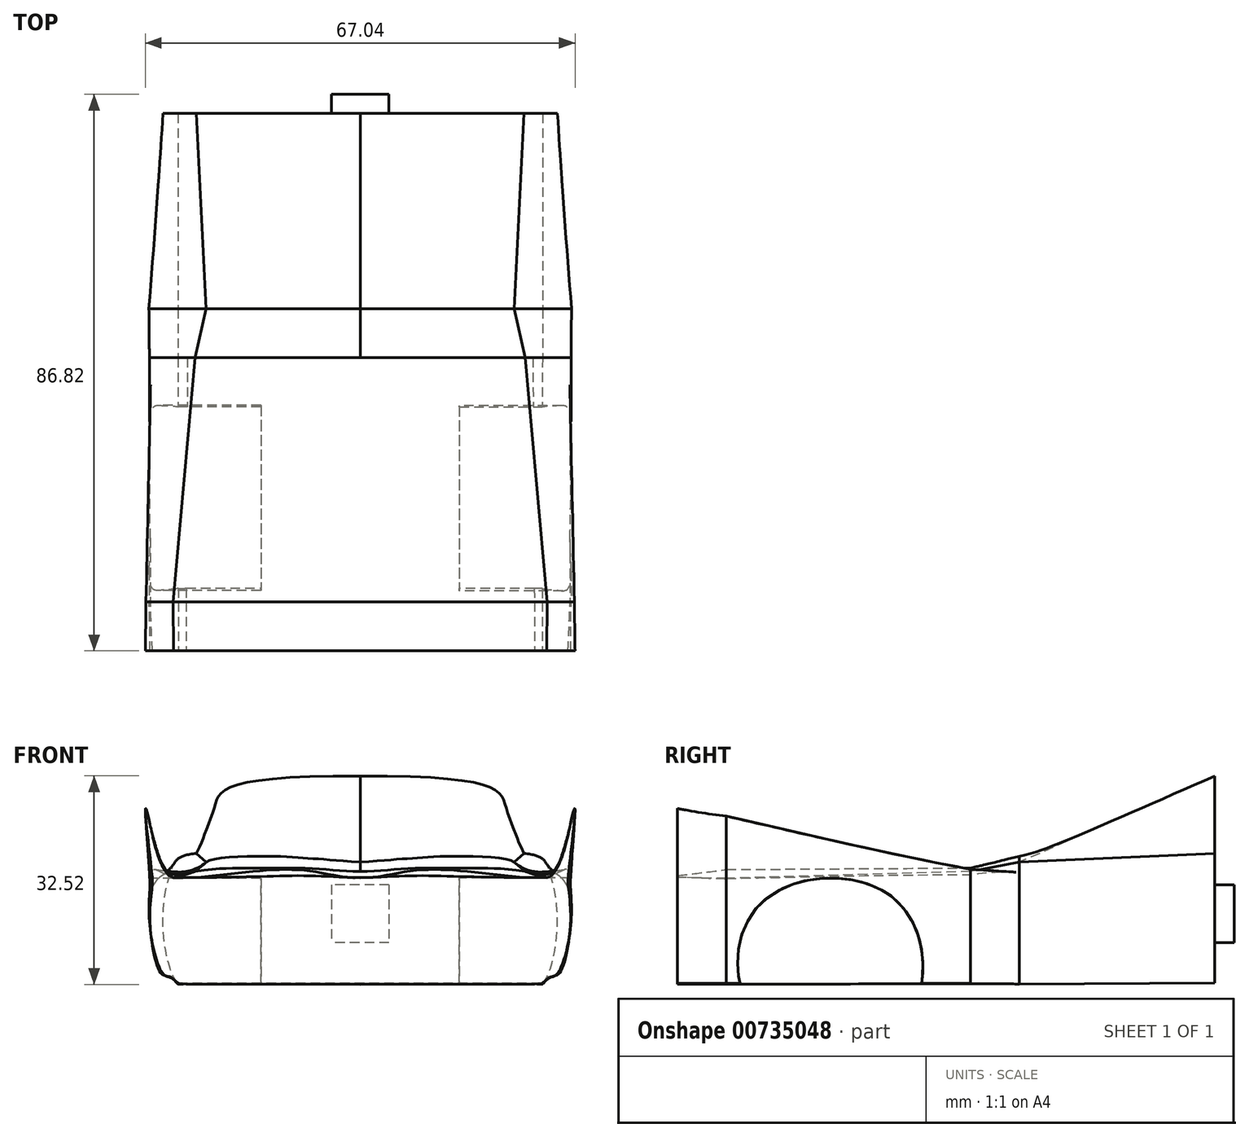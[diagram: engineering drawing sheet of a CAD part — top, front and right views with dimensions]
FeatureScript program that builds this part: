
annotation { "Feature Type Name" : "Feature", "Feature Type Description" : "" }
export const myFeature = defineFeature(function(context is Context, id is Id, definition is map)
    precondition{}
    {
        {
            var Q0;
            Q0=qCreatedBy(makeId("Front.planeOp"),FACE);
            var sketch = newSketch(context, id + "F0", { "sketchPlane" : qUnion([Q0])});
            skLineSegment(sketch, "E0", {"start": v(0, -180.47) * mm, "end": v(448.71, -180.47) * mm});
            skLineSegment(sketch, "E1", {"start": v(0, 357.9) * mm, "end": v(0, -180.47) * mm});
            skFitSpline(sketch, "E2", {"points": [v(448.71, -180.47) * mm, v(474.16, -180.47) * mm, v(512.73, -30.33) * mm, v(489.93, 116.8) * mm, v(425.94, 156.85) * mm], "startDerivative": vector(218.59, -88.61) * mm, "endDerivative": vector(-639.63, 77.65) * mm});
            skFitSpline(sketch, "E3", {"points": [v(425.94, 156.85) * mm, v(403.5, 209.2) * mm, v(380.6, 271.65) * mm, v(367.32, 306.69) * mm, v(0, 357.9) * mm], "startDerivative": vector(-217.52, 427.03) * mm, "endDerivative": vector(-1727.63, -7.94) * mm});
            skFitSpline(sketch, "E4.MirrorCS", {"points": [v(-448.71, -180.47) * mm, v(-474.16, -180.47) * mm, v(-512.73, -30.33) * mm, v(-489.93, 116.8) * mm, v(-425.94, 156.85) * mm], "startDerivative": vector(-218.59, -88.61) * mm, "endDerivative": vector(639.63, 77.65) * mm});
            skLineSegment(sketch, "E5.MirrorCS", {"start": v(0, -180.47) * mm, "end": v(-448.71, -180.47) * mm});
            skFitSpline(sketch, "E6.MirrorCS", {"points": [v(-425.94, 156.85) * mm, v(-403.5, 209.2) * mm, v(-380.6, 271.65) * mm, v(-367.32, 306.69) * mm, v(0, 357.9) * mm], "startDerivative": vector(217.52, 427.03) * mm, "endDerivative": vector(1727.63, -7.94) * mm});
            skLineSegment(sketch, "E7", {"start": v(-474.16, -180.47) * mm, "end": v(-448.71, -180.47) * mm});
            skLineSegment(sketch, "E8", {"start": v(448.71, -180.47) * mm, "end": v(474.16, -180.47) * mm});
            skSolve(sketch);
        }
        {
            var Q0;
            Q0=qCreatedBy(makeId("Front.planeOp"),FACE);
            cPlane(context, id + "F1", {"entities" : qUnion([Q0]), "cplaneType" : CPlaneType.OFFSET, "offset" : 508 * mm, "width" : 152.4 * mm, "height" : 152.4 * mm});
        }
        {
            var Q0;
            Q0=qCreatedBy(makeId("Front.planeOp"),FACE);
            cPlane(context, id + "F2", {"entities" : qUnion([Q0]), "cplaneType" : CPlaneType.OFFSET, "offset" : 635 * mm, "width" : 152.4 * mm, "height" : 152.4 * mm});
        }
        {
            var Q0;
            Q0=qCreatedBy(id+"F1.planeOp",FACE);
            var sketch = newSketch(context, id + "F3", { "sketchPlane" : qUnion([Q0])});
            skLineSegment(sketch, "E9", {"start": v(0, 133.83) * mm, "end": v(0, -182.92) * mm});
            skFitSpline(sketch, "E10.MirrorCS", {"points": [v(-448.71, -182.92) * mm, v(-474.16, -182.92) * mm, v(-491.12, -164.14) * mm, v(-514.1, -158.39) * mm, v(-547.21, -29.9) * mm, v(-541.48, 63.2) * mm, v(-504, 104.7) * mm, v(-400.3, 133.83) * mm], "startDerivative": vector(-218.59, -88.61) * mm, "endDerivative": vector(648.45, 573.05) * mm});
            skLineSegment(sketch, "E11.MirrorCS", {"start": v(0, -182.92) * mm, "end": v(-448.71, -182.92) * mm});
            skLineSegment(sketch, "E12", {"start": v(-474.16, -182.92) * mm, "end": v(-448.71, -182.92) * mm});
            skFitSpline(sketch, "E13", {"points": [v(-400.3, 133.83) * mm, v(-239.64, 149.35) * mm, v(-131.91, 143.87) * mm, v(0, 133.83) * mm], "startDerivative": vector(74.57, 104.4) * mm, "endDerivative": vector(567.18, -45.68) * mm});
            skLineSegment(sketch, "E14.MirrorCS", {"start": v(474.16, -182.92) * mm, "end": v(448.71, -182.92) * mm});
            skFitSpline(sketch, "E15.MirrorCS", {"points": [v(448.71, -182.92) * mm, v(474.16, -182.92) * mm, v(491.12, -164.14) * mm, v(514.1, -158.39) * mm, v(547.21, -29.9) * mm, v(541.48, 63.2) * mm, v(504, 104.7) * mm, v(400.3, 133.83) * mm], "startDerivative": vector(218.59, -88.61) * mm, "endDerivative": vector(-648.45, 573.05) * mm});
            skFitSpline(sketch, "E16.MirrorCS", {"points": [v(400.3, 133.83) * mm, v(239.64, 149.35) * mm, v(131.91, 143.87) * mm, v(0, 133.83) * mm], "startDerivative": vector(-74.57, 104.4) * mm, "endDerivative": vector(-567.18, -45.68) * mm});
            skLineSegment(sketch, "E17.MirrorCS", {"start": v(0, -182.92) * mm, "end": v(448.71, -182.92) * mm});
            skSolve(sketch);
        }
        {
            var Q0;
            Q0=qCreatedBy(id+"F2.planeOp",FACE);
            var sketch = newSketch(context, id + "F4", { "sketchPlane" : qUnion([Q0])});
            skLineSegment(sketch, "E18", {"start": v(0, 109.6) * mm, "end": v(0, -181.93) * mm});
            skFitSpline(sketch, "E19.MirrorCS", {"points": [v(-449.19, -181.93) * mm, v(-474, -181.58) * mm, v(-491.27, -163.37) * mm, v(-513.7, -157.3) * mm, v(-546.63, -32.12) * mm, v(-548.21, 0) * mm, v(-546.62, 31.6) * mm, v(-544.14, 61.05) * mm, v(-538.66, 114.09) * mm, v(-429.3, 109.6) * mm], "startDerivative": vector(-218.9, -88.74) * mm, "endDerivative": vector(1400.11, 441.1) * mm});
            skLineSegment(sketch, "E20.MirrorCS", {"start": v(0, -181.93) * mm, "end": v(-449.19, -181.93) * mm});
            skLineSegment(sketch, "E21", {"start": v(-474, -181.58) * mm, "end": v(-449.19, -181.93) * mm});
            skFitSpline(sketch, "E22", {"points": [v(-429.3, 109.6) * mm, v(-287.19, 117.98) * mm, v(-130.98, 117.58) * mm, v(0, 109.6) * mm], "startDerivative": vector(569.28, 88.84) * mm, "endDerivative": vector(425.94, 0) * mm});
            skLineSegment(sketch, "E23.MirrorCS", {"start": v(474, -181.58) * mm, "end": v(449.19, -181.93) * mm});
            skFitSpline(sketch, "E24.MirrorCS", {"points": [v(449.19, -181.93) * mm, v(474, -181.58) * mm, v(491.27, -163.37) * mm, v(513.7, -157.3) * mm, v(546.63, -32.12) * mm, v(548.21, 0) * mm, v(546.62, 31.6) * mm, v(544.14, 61.05) * mm, v(538.66, 114.09) * mm, v(429.3, 109.6) * mm], "startDerivative": vector(218.9, -88.74) * mm, "endDerivative": vector(-1400.11, 441.1) * mm});
            skFitSpline(sketch, "E25.MirrorCS", {"points": [v(429.3, 109.6) * mm, v(287.19, 117.98) * mm, v(130.98, 117.58) * mm, v(0, 109.6) * mm], "startDerivative": vector(-569.28, 88.84) * mm, "endDerivative": vector(-425.94, 0) * mm});
            skLineSegment(sketch, "E26.MirrorCS", {"start": v(0, -181.93) * mm, "end": v(449.19, -181.93) * mm});
            skSolve(sketch);
        }
        {
            var Q0;
            Q0=qCreatedBy(makeId("Right.planeOp"),FACE);
            cPlane(context, id + "F5", {"entities" : qUnion([Q0]), "cplaneType" : CPlaneType.OFFSET, "offset" : 508 * mm, "width" : 152.4 * mm, "height" : 152.4 * mm});
        }
        {
            var Q0;
            Q0=qCreatedBy(makeId("Right.planeOp"),FACE);
            cPlane(context, id + "F6", {"entities" : qUnion([Q0]), "cplaneType" : CPlaneType.OFFSET, "offset" : 508 * mm, "oppositeDirection" : true, "width" : 152.4 * mm, "height" : 152.4 * mm});
        }
        {
            var Q0;
            Q0=qCreatedBy(makeId("Front.planeOp"),FACE);
            cPlane(context, id + "F7", {"entities" : qUnion([Q0]), "cplaneType" : CPlaneType.OFFSET, "offset" : 1270 * mm, "width" : 152.4 * mm, "height" : 152.4 * mm});
        }
        {
            var Q0;
            Q0=qCreatedBy(id+"F7.planeOp",FACE);
            var sketch = newSketch(context, id + "F8", { "sketchPlane" : qUnion([Q0])});
            skLineSegment(sketch, "E27", {"start": v(0, 91.5) * mm, "end": v(0, -183.98) * mm});
            skFitSpline(sketch, "E28.MirrorCS", {"points": [v(-452.92, -183.74) * mm, v(-472.93, -181.46) * mm, v(-492.24, -166.6) * mm, v(-510.49, -159.07) * mm, v(-546.25, -34.03) * mm, v(-546.12, 75) * mm, v(-546.26, 106.31) * mm, v(-554.72, 252.87) * mm, v(-486.18, 91.5) * mm], "startDerivative": vector(-218.66, -88.64) * mm, "endDerivative": vector(445.88, 150.43) * mm});
            skLineSegment(sketch, "E29.MirrorCS", {"start": v(0, -183.98) * mm, "end": v(-452.92, -183.74) * mm});
            skLineSegment(sketch, "E30", {"start": v(-472.93, -181.46) * mm, "end": v(-452.92, -183.74) * mm});
            skFitSpline(sketch, "E31", {"points": [v(-486.18, 91.5) * mm, v(-291.63, 108.18) * mm, v(-132.85, 111.3) * mm, v(0, 91.5) * mm], "startDerivative": vector(425.94, 0) * mm, "endDerivative": vector(425.94, 0) * mm});
            skLineSegment(sketch, "E32.MirrorCS", {"start": v(472.93, -181.46) * mm, "end": v(452.92, -183.74) * mm});
            skFitSpline(sketch, "E33.MirrorCS", {"points": [v(452.92, -183.74) * mm, v(472.93, -181.46) * mm, v(492.24, -166.6) * mm, v(510.49, -159.07) * mm, v(546.25, -34.03) * mm, v(546.12, 75) * mm, v(546.26, 106.31) * mm, v(554.72, 252.87) * mm, v(486.18, 91.5) * mm], "startDerivative": vector(218.66, -88.64) * mm, "endDerivative": vector(-445.88, 150.43) * mm});
            skFitSpline(sketch, "E34.MirrorCS", {"points": [v(486.18, 91.5) * mm, v(291.63, 108.18) * mm, v(132.85, 111.3) * mm, v(0, 91.5) * mm], "startDerivative": vector(-425.94, 0) * mm, "endDerivative": vector(-425.94, 0) * mm});
            skLineSegment(sketch, "E35.MirrorCS", {"start": v(0, -183.98) * mm, "end": v(452.92, -183.74) * mm});
            skSolve(sketch);
        }
        {
            var Q0;
            Q0=qCreatedBy(makeId("Front.planeOp"),FACE);
            cPlane(context, id + "F9", {"entities" : qUnion([Q0]), "cplaneType" : CPlaneType.OFFSET, "offset" : 1397 * mm, "width" : 152.4 * mm, "height" : 152.4 * mm});
        }
        {
            var Q0;
            Q0=qCreatedBy(id+"F9.planeOp",FACE);
            var sketch = newSketch(context, id + "F10", { "sketchPlane" : qUnion([Q0])});
            skLineSegment(sketch, "E36", {"start": v(0, 93.84) * mm, "end": v(0, -183.21) * mm});
            skFitSpline(sketch, "E37.MirrorCS", {"points": [v(-452.87, -182.98) * mm, v(-472.94, -180.72) * mm, v(-492.23, -165.82) * mm, v(-510.52, -158.3) * mm, v(-546.25, -33.27) * mm, v(-540.97, 72.5) * mm, v(-543.72, 125.49) * mm, v(-558.42, 272.5) * mm, v(-551.07, 253.2) * mm, v(-485.29, 93.84) * mm], "startDerivative": vector(-218.66, -88.64) * mm, "endDerivative": vector(643.25, -140.85) * mm});
            skLineSegment(sketch, "E38.MirrorCS", {"start": v(0, -183.21) * mm, "end": v(-452.87, -182.98) * mm});
            skLineSegment(sketch, "E39", {"start": v(-472.94, -180.72) * mm, "end": v(-452.87, -182.98) * mm});
            skFitSpline(sketch, "E40", {"points": [v(-485.29, 93.84) * mm, v(-288.19, 95.7) * mm, v(-134.55, 98.5) * mm, v(0, 93.84) * mm], "startDerivative": vector(425.94, 0) * mm, "endDerivative": vector(425.94, 0) * mm});
            skLineSegment(sketch, "E41.MirrorCS", {"start": v(472.94, -180.72) * mm, "end": v(452.87, -182.98) * mm});
            skFitSpline(sketch, "E42.MirrorCS", {"points": [v(452.87, -182.98) * mm, v(472.94, -180.72) * mm, v(492.23, -165.82) * mm, v(510.52, -158.3) * mm, v(546.25, -33.27) * mm, v(540.97, 72.5) * mm, v(543.72, 125.49) * mm, v(558.42, 272.5) * mm, v(551.07, 253.2) * mm, v(485.29, 93.84) * mm], "startDerivative": vector(218.66, -88.64) * mm, "endDerivative": vector(-643.25, -140.85) * mm});
            skFitSpline(sketch, "E43.MirrorCS", {"points": [v(485.29, 93.84) * mm, v(288.19, 95.7) * mm, v(134.55, 98.5) * mm, v(0, 93.84) * mm], "startDerivative": vector(-425.94, 0) * mm, "endDerivative": vector(-425.94, 0) * mm});
            skLineSegment(sketch, "E44.MirrorCS", {"start": v(0, -183.21) * mm, "end": v(452.87, -182.98) * mm});
            skSolve(sketch);
        }
        {
            var Q0;
            Q0=makeQuery(id+"F0.imprint","IMPRINT",FACE,{"disambiguationData":[TD([[makeQuery(id+"F0.imprint","IMPRINT",EDGE,{"derivedFrom":sQuery(id+"F0.wireOp",EDGE,"E0")}),1.0]])]});
            var Q1;
            Q1=makeQuery(id+"F3.imprint","IMPRINT",FACE,{"disambiguationData":[TD([[makeQuery(id+"F3.imprint","IMPRINT",EDGE,{"derivedFrom":sQuery(id+"F3.wireOp",EDGE,"E9")}),1.0]])]});
            loft(context, id + "F11", {"sheetProfilesArray" : [{ "sheetProfileEntities" : qUnion([Q0]) }, { "sheetProfileEntities" : qUnion([Q1]) }]});
        }
        {
            var Q1;
            Q1=makeQuery(id+"F0.imprint","IMPRINT",FACE,{"disambiguationData":[TD([[makeQuery(id+"F0.imprint","IMPRINT",EDGE,{"derivedFrom":sQuery(id+"F0.wireOp",EDGE,"E1")}),-1.0]])]});
            var Q2;
            Q2=makeQuery(id+"F3.imprint","IMPRINT",FACE,{"disambiguationData":[TD([[makeQuery(id+"F3.imprint","IMPRINT",EDGE,{"derivedFrom":sQuery(id+"F3.wireOp",EDGE,"E9")}),-1.0]])]});
            loft(context, id + "F12", {"operationType" : NewBodyOperationType.ADD, "sheetProfilesArray" : [{ "sheetProfileEntities" : qUnion([Q1]) }, { "sheetProfileEntities" : qUnion([Q2]) }]});
        }
        {
            var Q1;
            Q1=makeQuery(id+"F3.imprint","IMPRINT",FACE,{"disambiguationData":[TD([[makeQuery(id+"F3.imprint","IMPRINT",EDGE,{"derivedFrom":sQuery(id+"F3.wireOp",EDGE,"E9")}),-1.0]])]});
            var Q2;
            Q2=makeQuery(id+"F4.imprint","IMPRINT",FACE,{"disambiguationData":[TD([[makeQuery(id+"F4.imprint","IMPRINT",EDGE,{"derivedFrom":sQuery(id+"F4.wireOp",EDGE,"E18")}),-1.0]])]});
            loft(context, id + "F13", {"operationType" : NewBodyOperationType.ADD, "sheetProfilesArray" : [{ "sheetProfileEntities" : qUnion([Q1]) }, { "sheetProfileEntities" : qUnion([Q2]) }]});
        }
        {
            var Q1;
            Q1=makeQuery(id+"F3.imprint","IMPRINT",FACE,{"disambiguationData":[TD([[makeQuery(id+"F3.imprint","IMPRINT",EDGE,{"derivedFrom":sQuery(id+"F3.wireOp",EDGE,"E9")}),1.0]])]});
            var Q2;
            Q2=makeQuery(id+"F4.imprint","IMPRINT",FACE,{"disambiguationData":[TD([[makeQuery(id+"F4.imprint","IMPRINT",EDGE,{"derivedFrom":sQuery(id+"F4.wireOp",EDGE,"E18")}),1.0]])]});
            loft(context, id + "F14", {"operationType" : NewBodyOperationType.ADD, "sheetProfilesArray" : [{ "sheetProfileEntities" : qUnion([Q1]) }, { "sheetProfileEntities" : qUnion([Q2]) }]});
        }
        {
            var Q1;
            Q1=makeQuery(id+"F4.imprint","IMPRINT",FACE,{"disambiguationData":[TD([[makeQuery(id+"F4.imprint","IMPRINT",EDGE,{"derivedFrom":sQuery(id+"F4.wireOp",EDGE,"E18")}),-1.0]])]});
            var Q2;
            Q2=makeQuery(id+"F8.imprint","IMPRINT",FACE,{"disambiguationData":[TD([[makeQuery(id+"F8.imprint","IMPRINT",EDGE,{"derivedFrom":sQuery(id+"F8.wireOp",EDGE,"E27")}),-1.0]])]});
            loft(context, id + "F15", {"operationType" : NewBodyOperationType.ADD, "sheetProfilesArray" : [{ "sheetProfileEntities" : qUnion([Q1]) }, { "sheetProfileEntities" : qUnion([Q2]) }]});
        }
        {
            var Q1;
            Q1=makeQuery(id+"F4.imprint","IMPRINT",FACE,{"disambiguationData":[TD([[makeQuery(id+"F4.imprint","IMPRINT",EDGE,{"derivedFrom":sQuery(id+"F4.wireOp",EDGE,"E18")}),1.0]])]});
            var Q2;
            Q2=makeQuery(id+"F8.imprint","IMPRINT",FACE,{"disambiguationData":[TD([[makeQuery(id+"F8.imprint","IMPRINT",EDGE,{"derivedFrom":sQuery(id+"F8.wireOp",EDGE,"E27")}),1.0]])]});
            loft(context, id + "F16", {"operationType" : NewBodyOperationType.ADD, "sheetProfilesArray" : [{ "sheetProfileEntities" : qUnion([Q1]) }, { "sheetProfileEntities" : qUnion([Q2]) }]});
        }
        {
            var Q1;
            Q1=makeQuery(id+"F8.imprint","IMPRINT",FACE,{"disambiguationData":[TD([[makeQuery(id+"F8.imprint","IMPRINT",EDGE,{"derivedFrom":sQuery(id+"F8.wireOp",EDGE,"E27")}),-1.0]])]});
            var Q2;
            Q2=makeQuery(id+"F10.imprint","IMPRINT",FACE,{"disambiguationData":[TD([[makeQuery(id+"F10.imprint","IMPRINT",EDGE,{"derivedFrom":sQuery(id+"F10.wireOp",EDGE,"E36")}),-1.0]])]});
            loft(context, id + "F17", {"operationType" : NewBodyOperationType.ADD, "sheetProfilesArray" : [{ "sheetProfileEntities" : qUnion([Q1]) }, { "sheetProfileEntities" : qUnion([Q2]) }]});
        }
        {
            var Q1;
            Q1=makeQuery(id+"F8.imprint","IMPRINT",FACE,{"disambiguationData":[TD([[makeQuery(id+"F8.imprint","IMPRINT",EDGE,{"derivedFrom":sQuery(id+"F8.wireOp",EDGE,"E27")}),1.0]])]});
            var Q2;
            Q2=makeQuery(id+"F10.imprint","IMPRINT",FACE,{"disambiguationData":[TD([[makeQuery(id+"F10.imprint","IMPRINT",EDGE,{"derivedFrom":sQuery(id+"F10.wireOp",EDGE,"E36")}),1.0]])]});
            loft(context, id + "F18", {"operationType" : NewBodyOperationType.ADD, "sheetProfilesArray" : [{ "sheetProfileEntities" : qUnion([Q1]) }, { "sheetProfileEntities" : qUnion([Q2]) }]});
        }
        {
            var Q0;
            Q0=qCreatedBy(id+"F5.planeOp",FACE);
            var sketch = newSketch(context, id + "F19", { "sketchPlane" : qUnion([Q0])});
            skFitSpline(sketch, "E45", {"points": [v(-1171.11, -297.1) * mm, v(-817.3, -293.58) * mm, v(-828.11, 34.08) * mm, v(-1185.47, 21.81) * mm, v(-1171.11, -297.1) * mm]});
            skSolve(sketch);
        }
        {
            var Q0;
            Q0=qCreatedBy(id+"F6.planeOp",FACE);
            var sketch = newSketch(context, id + "F20", { "sketchPlane" : qUnion([Q0])});
            skFitSpline(sketch, "E46", {"points": [v(-1170.51, -298) * mm, v(-816.7, -294.47) * mm, v(-827.51, 33.19) * mm, v(-1184.87, 20.92) * mm, v(-1170.51, -298) * mm]});
            skSolve(sketch);
        }
        {
            var Q0;
            Q0=qCreatedBy(makeId("Front.planeOp"),FACE);
            var sketch = newSketch(context, id + "F21", { "sketchPlane" : qUnion([Q0])});
            skLineSegment(sketch, "E47.bottom", {"start": v(75, 75) * mm, "end": v(-75, 75) * mm});
            skLineSegment(sketch, "E47.top", {"start": v(75, -75) * mm, "end": v(-75, -75) * mm});
            skLineSegment(sketch, "E47.left", {"start": v(75, 75) * mm, "end": v(75, -75) * mm});
            skLineSegment(sketch, "E47.right", {"start": v(-75, 75) * mm, "end": v(-75, -75) * mm});
            skPoint(sketch, "E47.middle", {"position": v(0, 0) * mm});
            skSolve(sketch);
        }
        {
            var Q0;
            Q0 = qSketchRegion(id + "F21", true);
            extrude(context, id + "F22", {"entities" : qUnion([Q0]), "operationType" : NewBodyOperationType.ADD, "oppositeDirection" : true, "depth" : 50 * mm, "offsetDistance" : 25 * mm});
        }
        {
            var Q0;
            Q0 = qSketchRegion(id + "F19", true);
            extrude(context, id + "F23", {"entities" : qUnion([Q0]), "operationType" : NewBodyOperationType.REMOVE, "depth" : 50 * mm, "offsetDistance" : 25 * mm});
        }
        {
            var Q0;
            Q0 = qSketchRegion(id + "F19", true);
            extrude(context, id + "F24", {"entities" : qUnion([Q0]), "operationType" : NewBodyOperationType.REMOVE, "oppositeDirection" : true, "depth" : 250 * mm, "offsetDistance" : 25 * mm});
        }
        {
            var Q0;
            Q0 = qSketchRegion(id + "F20", true);
            extrude(context, id + "F25", {"entities" : qUnion([Q0]), "operationType" : NewBodyOperationType.REMOVE, "oppositeDirection" : true, "depth" : 50 * mm, "offsetDistance" : 25 * mm});
        }
        {
            var Q0;
            Q0 = qSketchRegion(id + "F20", true);
            extrude(context, id + "F26", {"entities" : qUnion([Q0]), "operationType" : NewBodyOperationType.REMOVE, "depth" : 250 * mm, "offsetDistance" : 25 * mm});
        }
        {
            var Q0;
            Q0=makeQuery(id+"F11.opLoft","SWEPT_BODY",BODY,{"disambiguationData":[OSD([makeQuery(id+"F0.imprint","IMPRINT",FACE,{"disambiguationData":[TD([[makeQuery(id+"F0.imprint","IMPRINT",EDGE,{"derivedFrom":sQuery(id+"F0.wireOp",EDGE,"E0")}),1.0]])]}),makeQuery(id+"F3.imprint","IMPRINT",FACE,{"disambiguationData":[TD([[makeQuery(id+"F3.imprint","IMPRINT",EDGE,{"derivedFrom":sQuery(id+"F3.wireOp",EDGE,"E9")}),1.0]])]})])]});
            var Q1;
            Q1=qCreatedBy(makeId("Origin.pointOp"),VERTEX);
            transform(context, id + "F27", {"entities" : qUnion([Q0]), "transformType" : TransformType.SCALE_UNIFORMLY, "scale" : 0.06, "scalePoint" : qUnion([Q1]), "makeCopy" : false});
        }
    });
